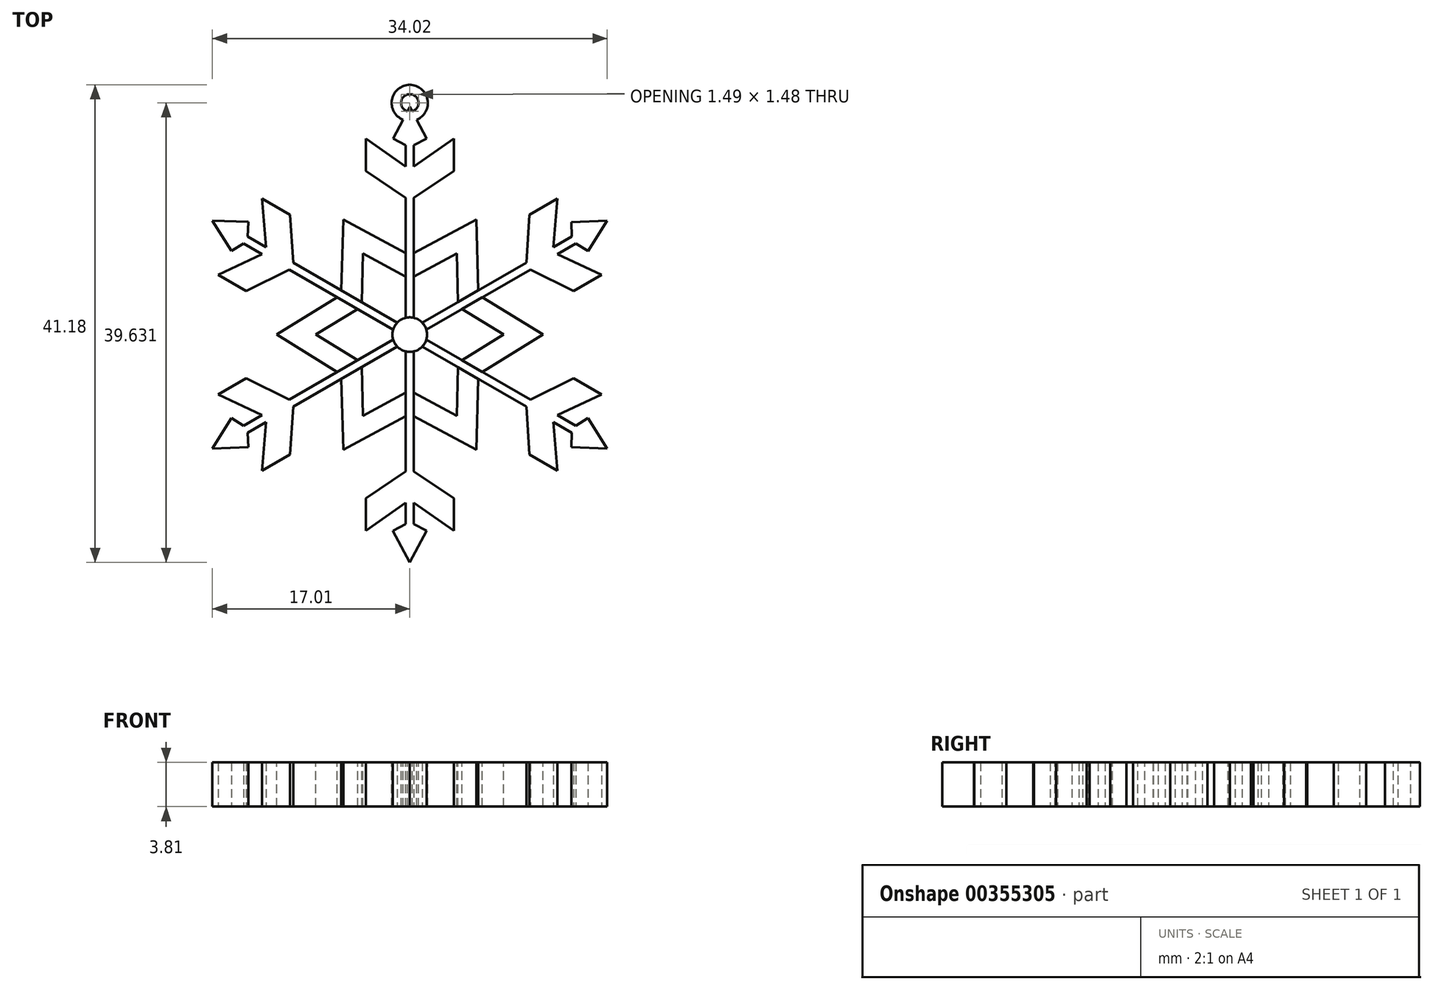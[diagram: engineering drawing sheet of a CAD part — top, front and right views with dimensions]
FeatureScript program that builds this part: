
annotation { "Feature Type Name" : "Feature", "Feature Type Description" : "" }
export const myFeature = defineFeature(function(context is Context, id is Id, definition is map)
    precondition{}
    {
        {
            var Q0;
            Q0=qCreatedBy(makeId("Top.planeOp"),FACE);
            var sketch = newSketch(context, id + "F0", { "sketchPlane" : qUnion([Q0])});
            skCircle(sketch, "E0", {"center": v(0, 0) * mm, "radius": 2.98 * mm});
            skLineSegment(sketch, "E1", {"start": v(0, -39.28) * mm, "end": v(2.88, -33.82) * mm});
            skLineSegment(sketch, "E2", {"start": v(2.88, -33.82) * mm, "end": v(-2.91, -33.82) * mm});
            skLineSegment(sketch, "E3", {"start": v(-2.91, -33.82) * mm, "end": v(0, -39.28) * mm});
            skLineSegment(sketch, "E4", {"start": v(0.7, -2.9) * mm, "end": v(0.7, -33.82) * mm});
            skLineSegment(sketch, "E5.MirrorCS", {"start": v(-0.7, -2.9) * mm, "end": v(-0.7, -33.82) * mm});
            skLineSegment(sketch, "E6", {"start": v(2.88, -33.82) * mm, "end": v(0.7, -32.67) * mm});
            skLineSegment(sketch, "E7", {"start": v(0.7, -29) * mm, "end": v(7.59, -33.78) * mm});
            skLineSegment(sketch, "E8", {"start": v(7.59, -33.78) * mm, "end": v(7.59, -28.23) * mm});
            skLineSegment(sketch, "E9", {"start": v(7.59, -28.23) * mm, "end": v(0.7, -23.6) * mm});
            skLineSegment(sketch, "E10.MirrorCS", {"start": v(-0.7, -29) * mm, "end": v(-7.59, -33.78) * mm});
            skLineSegment(sketch, "E11.MirrorCS", {"start": v(-7.59, -28.23) * mm, "end": v(-0.7, -23.6) * mm});
            skLineSegment(sketch, "E12.MirrorCS", {"start": v(-7.59, -33.78) * mm, "end": v(-7.59, -28.23) * mm});
            skLineSegment(sketch, "E13.MirrorCS", {"start": v(-2.88, -33.82) * mm, "end": v(-0.7, -32.67) * mm});
            skSolve(sketch);
        }
        {
            var Q0;
            Q0=qCreatedBy(makeId("Right.planeOp"),FACE);
            var sketch = newSketch(context, id + "F1", { "sketchPlane" : qUnion([Q0])});
            skLineSegment(sketch, "E14", {"start": v(0, 27.35) * mm, "end": v(0, -20.93) * mm});
            skSolve(sketch);
        }
        {
            var Q0;
            {var subQ0=sQuery(id+"F0.wireOp",EDGE,"E4");var subQ1=sQuery(id+"F0.wireOp",EDGE,"E0");var subQ2=makeQuery(id+"F0.imprint","INTERSECT",VERTEX,{"derivedFrom":[subQ1,subQ0]});Q0=makeQuery(id+"F0.imprint","IMPRINT",FACE,{"disambiguationData":[TD([[makeQuery(id+"F0.imprint","IMPRINT",EDGE,{"disambiguationData":[TD([[subQ2,1.0]])],"derivedFrom":subQ1}),-1.0]])]});}
            var Q1;
            {var subQ0=sQuery(id+"F0.wireOp",EDGE,"E10.MirrorCS");Q1=makeQuery(id+"F0.imprint","IMPRINT",FACE,{"disambiguationData":[TD([[makeQuery(id+"F0.imprint","IMPRINT",EDGE,{"derivedFrom":subQ0}),-1.0]])]});}
            var Q2;
            {var subQ0=sQuery(id+"F0.wireOp",EDGE,"E7");Q2=makeQuery(id+"F0.imprint","IMPRINT",FACE,{"disambiguationData":[TD([[makeQuery(id+"F0.imprint","IMPRINT",EDGE,{"derivedFrom":subQ0}),1.0]])]});}
            var Q3;
            {var subQ4=sQuery(id+"F0.wireOp",EDGE,"E1");Q3=makeQuery(id+"F0.imprint","IMPRINT",FACE,{"disambiguationData":[TD([[makeQuery(id+"F0.imprint","IMPRINT",EDGE,{"derivedFrom":subQ4}),1.0]])]});}
            var Q4;
            {var subQ0=sQuery(id+"F0.wireOp",EDGE,"E6");Q4=makeQuery(id+"F0.imprint","IMPRINT",FACE,{"disambiguationData":[TD([[makeQuery(id+"F0.imprint","IMPRINT",EDGE,{"derivedFrom":subQ0}),1.0]])]});}
            var Q5;
            {var subQ3=sQuery(id+"F0.wireOp",EDGE,"E13.MirrorCS");Q5=makeQuery(id+"F0.imprint","IMPRINT",FACE,{"disambiguationData":[TD([[makeQuery(id+"F0.imprint","IMPRINT",EDGE,{"derivedFrom":subQ3}),-1.0]])]});}
            extrude(context, id + "F2", {"entities" : qUnion([Q0, Q1, Q2, Q3, Q4, Q5]), "depth" : 7.62 * mm});
        }
        {
            var Q0;
            Q0=makeQuery(id+"F2.opExtrude","SWEPT_BODY",BODY,{"disambiguationData":[OSD([sQuery(id+"F0.wireOp",EDGE,"E0"),sQuery(id+"F0.wireOp",EDGE,"E1"),sQuery(id+"F0.wireOp",EDGE,"E2"),sQuery(id+"F0.wireOp",EDGE,"E3"),sQuery(id+"F0.wireOp",EDGE,"E4"),sQuery(id+"F0.wireOp",EDGE,"E5.MirrorCS"),sQuery(id+"F0.wireOp",EDGE,"E6"),sQuery(id+"F0.wireOp",EDGE,"E7"),sQuery(id+"F0.wireOp",EDGE,"E8"),sQuery(id+"F0.wireOp",EDGE,"E9"),sQuery(id+"F0.wireOp",EDGE,"E10.MirrorCS"),sQuery(id+"F0.wireOp",EDGE,"E11.MirrorCS"),sQuery(id+"F0.wireOp",EDGE,"E12.MirrorCS"),sQuery(id+"F0.wireOp",EDGE,"E13.MirrorCS")])]});
            var Q1;
            Q1=sQuery(id+"F1.wireOp",EDGE,"E14");
            circularPattern(context, id + "F3", {"entities" : qUnion([Q0]), "axis" : qUnion([Q1]), "angle" : 360 * degree, "instanceCount" : 6, "equalSpace" : true});
        }
        {
            var Q0;
            Q0=makeQuery(id+"F3.opPattern","COPY",FACE,{"derivedFrom":makeQuery(id+"F2.opExtrude","CAP_FACE",FACE,{"disambiguationData":[OSD([sQuery(id+"F0.wireOp",EDGE,"E0"),sQuery(id+"F0.wireOp",EDGE,"E1"),sQuery(id+"F0.wireOp",EDGE,"E2"),sQuery(id+"F0.wireOp",EDGE,"E3"),sQuery(id+"F0.wireOp",EDGE,"E4"),sQuery(id+"F0.wireOp",EDGE,"E5.MirrorCS"),sQuery(id+"F0.wireOp",EDGE,"E6"),sQuery(id+"F0.wireOp",EDGE,"E7"),sQuery(id+"F0.wireOp",EDGE,"E8"),sQuery(id+"F0.wireOp",EDGE,"E9"),sQuery(id+"F0.wireOp",EDGE,"E10.MirrorCS"),sQuery(id+"F0.wireOp",EDGE,"E11.MirrorCS"),sQuery(id+"F0.wireOp",EDGE,"E12.MirrorCS"),sQuery(id+"F0.wireOp",EDGE,"E13.MirrorCS")])],"isStart":false}),"instanceName":"1"});
            var sketch = newSketch(context, id + "F4", { "sketchPlane" : qUnion([Q0])});
            skLineSegment(sketch, "E15", {"start": v(-22.94, 0) * mm, "end": v(-12.52, -6.42) * mm});
            skLineSegment(sketch, "E16", {"start": v(-12.52, -6.42) * mm, "end": v(-8.99, -4.38) * mm});
            skLineSegment(sketch, "E17", {"start": v(-8.99, -4.38) * mm, "end": v(-16.2, 0) * mm});
            skLineSegment(sketch, "E18.MirrorCS", {"start": v(-22.94, 0) * mm, "end": v(-12.52, 6.42) * mm});
            skLineSegment(sketch, "E19.MirrorCS", {"start": v(-8.99, 4.38) * mm, "end": v(-16.2, 0) * mm});
            skLineSegment(sketch, "E20.MirrorCS", {"start": v(-12.52, 6.42) * mm, "end": v(-8.99, 4.38) * mm});
            skSolve(sketch);
        }
        {
            var Q0;
            Q0=makeQuery(id+"F4.imprint","IMPRINT",FACE,{"disambiguationData":[TD([[makeQuery(id+"F4.imprint","IMPRINT",EDGE,{"derivedFrom":sQuery(id+"F4.wireOp",EDGE,"E15")}),1.0]])]});
            extrude(context, id + "F5", {"entities" : qUnion([Q0]), "oppositeDirection" : true, "depth" : 7.62 * mm});
        }
        {
            var Q0;
            Q0=makeQuery(id+"F5.opExtrude","SWEPT_BODY",BODY,{"disambiguationData":[OSD([sQuery(id+"F4.wireOp",EDGE,"E15"),sQuery(id+"F4.wireOp",EDGE,"E16"),sQuery(id+"F4.wireOp",EDGE,"E17"),sQuery(id+"F4.wireOp",EDGE,"E18.MirrorCS"),sQuery(id+"F4.wireOp",EDGE,"E19.MirrorCS"),sQuery(id+"F4.wireOp",EDGE,"E20.MirrorCS")])]});
            var Q1;
            Q1=sQuery(id+"F1.wireOp",EDGE,"E14");
            circularPattern(context, id + "F6", {"entities" : qUnion([Q0]), "axis" : qUnion([Q1]), "angle" : 360 * degree, "instanceCount" : 6, "equalSpace" : true});
        }
        {
            var Q0;
            Q0=makeQuery(id+"F3.opPattern","COPY",FACE,{"derivedFrom":makeQuery(id+"F2.opExtrude","CAP_FACE",FACE,{"disambiguationData":[OSD([sQuery(id+"F0.wireOp",EDGE,"E0"),sQuery(id+"F0.wireOp",EDGE,"E1"),sQuery(id+"F0.wireOp",EDGE,"E2"),sQuery(id+"F0.wireOp",EDGE,"E3"),sQuery(id+"F0.wireOp",EDGE,"E4"),sQuery(id+"F0.wireOp",EDGE,"E5.MirrorCS"),sQuery(id+"F0.wireOp",EDGE,"E6"),sQuery(id+"F0.wireOp",EDGE,"E7"),sQuery(id+"F0.wireOp",EDGE,"E8"),sQuery(id+"F0.wireOp",EDGE,"E9"),sQuery(id+"F0.wireOp",EDGE,"E10.MirrorCS"),sQuery(id+"F0.wireOp",EDGE,"E11.MirrorCS"),sQuery(id+"F0.wireOp",EDGE,"E12.MirrorCS"),sQuery(id+"F0.wireOp",EDGE,"E13.MirrorCS")])],"isStart":false}),"instanceName":"3"});
            var sketch = newSketch(context, id + "F7", { "sketchPlane" : qUnion([Q0])});
            skCircle(sketch, "E21", {"center": v(0, 39.95) * mm, "radius": 1.5 * mm});
            skCircle(sketch, "E22", {"center": v(0, 39.95) * mm, "radius": 3.12 * mm});
            skSolve(sketch);
        }
        {
            var Q0;
            {var subQ0=sQuery(id+"F7.wireOp",EDGE,"E21");var subQ1=makeQuery(id+"F3.opPattern","COPY",EDGE,{"derivedFrom":makeQuery(id+"F2.opExtrude","CAP_EDGE",EDGE,{"disambiguationData":[OSD([sQuery(id+"F0.wireOp",EDGE,"E1")])],"isStart":false}),"instanceName":"3"});var subQ2=makeQuery(id+"F7.imprint","INTERSECT",VERTEX,{"derivedFrom":[subQ1,subQ0]});Q0=makeQuery(id+"F7.imprint","IMPRINT",FACE,{"disambiguationData":[TD([[makeQuery(id+"F7.imprint","IMPRINT",EDGE,{"disambiguationData":[TD([[subQ2,1.0]])],"derivedFrom":subQ0}),-1.0]])]});}
            extrude(context, id + "F8", {"entities" : qUnion([Q0]), "operationType" : NewBodyOperationType.ADD, "oppositeDirection" : true, "depth" : 7.62 * mm});
        }
        {
            var Q0;
            {var subQ0=sQuery(id+"F0.wireOp",EDGE,"E0");var subQ1=makeQuery(id+"F0.imprint","INTERSECT",VERTEX,{"derivedFrom":[subQ0,sQuery(id+"F0.wireOp",EDGE,"E4")]});Q0=makeQuery(id+"F0.imprint","IMPRINT",FACE,{"disambiguationData":[TD([[makeQuery(id+"F0.imprint","IMPRINT",EDGE,{"disambiguationData":[TD([[subQ1,1.0]])],"derivedFrom":subQ0}),1.0]])]});}
            extrude(context, id + "F9", {"entities" : qUnion([Q0]), "depth" : 7.62 * mm});
        }
        {
            var Q0;
            Q0=makeQuery(id+"F3.opPattern","COPY",BODY,{"derivedFrom":makeQuery(id+"F2.opExtrude","SWEPT_BODY",BODY,{"disambiguationData":[OSD([sQuery(id+"F0.wireOp",EDGE,"E0"),sQuery(id+"F0.wireOp",EDGE,"E1"),sQuery(id+"F0.wireOp",EDGE,"E2"),sQuery(id+"F0.wireOp",EDGE,"E3"),sQuery(id+"F0.wireOp",EDGE,"E4"),sQuery(id+"F0.wireOp",EDGE,"E5.MirrorCS"),sQuery(id+"F0.wireOp",EDGE,"E6"),sQuery(id+"F0.wireOp",EDGE,"E7"),sQuery(id+"F0.wireOp",EDGE,"E8"),sQuery(id+"F0.wireOp",EDGE,"E9"),sQuery(id+"F0.wireOp",EDGE,"E10.MirrorCS"),sQuery(id+"F0.wireOp",EDGE,"E11.MirrorCS"),sQuery(id+"F0.wireOp",EDGE,"E12.MirrorCS"),sQuery(id+"F0.wireOp",EDGE,"E13.MirrorCS")])]}),"instanceName":"3"});
            var Q1;
            Q1=makeQuery(id+"F6.opPattern","COPY",BODY,{"derivedFrom":makeQuery(id+"F5.opExtrude","SWEPT_BODY",BODY,{"disambiguationData":[OSD([sQuery(id+"F4.wireOp",EDGE,"E15"),sQuery(id+"F4.wireOp",EDGE,"E16"),sQuery(id+"F4.wireOp",EDGE,"E17"),sQuery(id+"F4.wireOp",EDGE,"E18.MirrorCS"),sQuery(id+"F4.wireOp",EDGE,"E19.MirrorCS"),sQuery(id+"F4.wireOp",EDGE,"E20.MirrorCS")])]}),"instanceName":"1"});
            var Q2;
            Q2=makeQuery(id+"F3.opPattern","COPY",BODY,{"derivedFrom":makeQuery(id+"F2.opExtrude","SWEPT_BODY",BODY,{"disambiguationData":[OSD([sQuery(id+"F0.wireOp",EDGE,"E0"),sQuery(id+"F0.wireOp",EDGE,"E1"),sQuery(id+"F0.wireOp",EDGE,"E2"),sQuery(id+"F0.wireOp",EDGE,"E3"),sQuery(id+"F0.wireOp",EDGE,"E4"),sQuery(id+"F0.wireOp",EDGE,"E5.MirrorCS"),sQuery(id+"F0.wireOp",EDGE,"E6"),sQuery(id+"F0.wireOp",EDGE,"E7"),sQuery(id+"F0.wireOp",EDGE,"E8"),sQuery(id+"F0.wireOp",EDGE,"E9"),sQuery(id+"F0.wireOp",EDGE,"E10.MirrorCS"),sQuery(id+"F0.wireOp",EDGE,"E11.MirrorCS"),sQuery(id+"F0.wireOp",EDGE,"E12.MirrorCS"),sQuery(id+"F0.wireOp",EDGE,"E13.MirrorCS")])]}),"instanceName":"2"});
            var Q3;
            Q3=makeQuery(id+"F5.opExtrude","SWEPT_BODY",BODY,{"disambiguationData":[OSD([sQuery(id+"F4.wireOp",EDGE,"E15"),sQuery(id+"F4.wireOp",EDGE,"E16"),sQuery(id+"F4.wireOp",EDGE,"E17"),sQuery(id+"F4.wireOp",EDGE,"E18.MirrorCS"),sQuery(id+"F4.wireOp",EDGE,"E19.MirrorCS"),sQuery(id+"F4.wireOp",EDGE,"E20.MirrorCS")])]});
            var Q4;
            Q4=makeQuery(id+"F3.opPattern","COPY",BODY,{"derivedFrom":makeQuery(id+"F2.opExtrude","SWEPT_BODY",BODY,{"disambiguationData":[OSD([sQuery(id+"F0.wireOp",EDGE,"E0"),sQuery(id+"F0.wireOp",EDGE,"E1"),sQuery(id+"F0.wireOp",EDGE,"E2"),sQuery(id+"F0.wireOp",EDGE,"E3"),sQuery(id+"F0.wireOp",EDGE,"E4"),sQuery(id+"F0.wireOp",EDGE,"E5.MirrorCS"),sQuery(id+"F0.wireOp",EDGE,"E6"),sQuery(id+"F0.wireOp",EDGE,"E7"),sQuery(id+"F0.wireOp",EDGE,"E8"),sQuery(id+"F0.wireOp",EDGE,"E9"),sQuery(id+"F0.wireOp",EDGE,"E10.MirrorCS"),sQuery(id+"F0.wireOp",EDGE,"E11.MirrorCS"),sQuery(id+"F0.wireOp",EDGE,"E12.MirrorCS"),sQuery(id+"F0.wireOp",EDGE,"E13.MirrorCS")])]}),"instanceName":"1"});
            var Q5;
            Q5=makeQuery(id+"F2.opExtrude","SWEPT_BODY",BODY,{"disambiguationData":[OSD([sQuery(id+"F0.wireOp",EDGE,"E0"),sQuery(id+"F0.wireOp",EDGE,"E1"),sQuery(id+"F0.wireOp",EDGE,"E2"),sQuery(id+"F0.wireOp",EDGE,"E3"),sQuery(id+"F0.wireOp",EDGE,"E4"),sQuery(id+"F0.wireOp",EDGE,"E5.MirrorCS"),sQuery(id+"F0.wireOp",EDGE,"E6"),sQuery(id+"F0.wireOp",EDGE,"E7"),sQuery(id+"F0.wireOp",EDGE,"E8"),sQuery(id+"F0.wireOp",EDGE,"E9"),sQuery(id+"F0.wireOp",EDGE,"E10.MirrorCS"),sQuery(id+"F0.wireOp",EDGE,"E11.MirrorCS"),sQuery(id+"F0.wireOp",EDGE,"E12.MirrorCS"),sQuery(id+"F0.wireOp",EDGE,"E13.MirrorCS")])]});
            var Q6;
            Q6=makeQuery(id+"F6.opPattern","COPY",BODY,{"derivedFrom":makeQuery(id+"F5.opExtrude","SWEPT_BODY",BODY,{"disambiguationData":[OSD([sQuery(id+"F4.wireOp",EDGE,"E15"),sQuery(id+"F4.wireOp",EDGE,"E16"),sQuery(id+"F4.wireOp",EDGE,"E17"),sQuery(id+"F4.wireOp",EDGE,"E18.MirrorCS"),sQuery(id+"F4.wireOp",EDGE,"E19.MirrorCS"),sQuery(id+"F4.wireOp",EDGE,"E20.MirrorCS")])]}),"instanceName":"4"});
            var Q7;
            Q7=makeQuery(id+"F6.opPattern","COPY",BODY,{"derivedFrom":makeQuery(id+"F5.opExtrude","SWEPT_BODY",BODY,{"disambiguationData":[OSD([sQuery(id+"F4.wireOp",EDGE,"E15"),sQuery(id+"F4.wireOp",EDGE,"E16"),sQuery(id+"F4.wireOp",EDGE,"E17"),sQuery(id+"F4.wireOp",EDGE,"E18.MirrorCS"),sQuery(id+"F4.wireOp",EDGE,"E19.MirrorCS"),sQuery(id+"F4.wireOp",EDGE,"E20.MirrorCS")])]}),"instanceName":"3"});
            var Q8;
            Q8=makeQuery(id+"F6.opPattern","COPY",BODY,{"derivedFrom":makeQuery(id+"F5.opExtrude","SWEPT_BODY",BODY,{"disambiguationData":[OSD([sQuery(id+"F4.wireOp",EDGE,"E15"),sQuery(id+"F4.wireOp",EDGE,"E16"),sQuery(id+"F4.wireOp",EDGE,"E17"),sQuery(id+"F4.wireOp",EDGE,"E18.MirrorCS"),sQuery(id+"F4.wireOp",EDGE,"E19.MirrorCS"),sQuery(id+"F4.wireOp",EDGE,"E20.MirrorCS")])]}),"instanceName":"2"});
            var Q9;
            Q9=makeQuery(id+"F3.opPattern","COPY",BODY,{"derivedFrom":makeQuery(id+"F2.opExtrude","SWEPT_BODY",BODY,{"disambiguationData":[OSD([sQuery(id+"F0.wireOp",EDGE,"E0"),sQuery(id+"F0.wireOp",EDGE,"E1"),sQuery(id+"F0.wireOp",EDGE,"E2"),sQuery(id+"F0.wireOp",EDGE,"E3"),sQuery(id+"F0.wireOp",EDGE,"E4"),sQuery(id+"F0.wireOp",EDGE,"E5.MirrorCS"),sQuery(id+"F0.wireOp",EDGE,"E6"),sQuery(id+"F0.wireOp",EDGE,"E7"),sQuery(id+"F0.wireOp",EDGE,"E8"),sQuery(id+"F0.wireOp",EDGE,"E9"),sQuery(id+"F0.wireOp",EDGE,"E10.MirrorCS"),sQuery(id+"F0.wireOp",EDGE,"E11.MirrorCS"),sQuery(id+"F0.wireOp",EDGE,"E12.MirrorCS"),sQuery(id+"F0.wireOp",EDGE,"E13.MirrorCS")])]}),"instanceName":"4"});
            var Q10;
            Q10=makeQuery(id+"F6.opPattern","COPY",BODY,{"derivedFrom":makeQuery(id+"F5.opExtrude","SWEPT_BODY",BODY,{"disambiguationData":[OSD([sQuery(id+"F4.wireOp",EDGE,"E15"),sQuery(id+"F4.wireOp",EDGE,"E16"),sQuery(id+"F4.wireOp",EDGE,"E17"),sQuery(id+"F4.wireOp",EDGE,"E18.MirrorCS"),sQuery(id+"F4.wireOp",EDGE,"E19.MirrorCS"),sQuery(id+"F4.wireOp",EDGE,"E20.MirrorCS")])]}),"instanceName":"5"});
            var Q11;
            Q11=makeQuery(id+"F3.opPattern","COPY",BODY,{"derivedFrom":makeQuery(id+"F2.opExtrude","SWEPT_BODY",BODY,{"disambiguationData":[OSD([sQuery(id+"F0.wireOp",EDGE,"E0"),sQuery(id+"F0.wireOp",EDGE,"E1"),sQuery(id+"F0.wireOp",EDGE,"E2"),sQuery(id+"F0.wireOp",EDGE,"E3"),sQuery(id+"F0.wireOp",EDGE,"E4"),sQuery(id+"F0.wireOp",EDGE,"E5.MirrorCS"),sQuery(id+"F0.wireOp",EDGE,"E6"),sQuery(id+"F0.wireOp",EDGE,"E7"),sQuery(id+"F0.wireOp",EDGE,"E8"),sQuery(id+"F0.wireOp",EDGE,"E9"),sQuery(id+"F0.wireOp",EDGE,"E10.MirrorCS"),sQuery(id+"F0.wireOp",EDGE,"E11.MirrorCS"),sQuery(id+"F0.wireOp",EDGE,"E12.MirrorCS"),sQuery(id+"F0.wireOp",EDGE,"E13.MirrorCS")])]}),"instanceName":"5"});
            var Q12;
            Q12=makeQuery(id+"F9.opExtrude","SWEPT_BODY",BODY,{"disambiguationData":[OSD([sQuery(id+"F0.wireOp",EDGE,"E0")])]});
            var Q13;
            Q13=sQuery(id+"F1.wireOp",VERTEX,"E14.end");
            transform(context, id + "F10", {"entities" : qUnion([Q0, Q1, Q2, Q3, Q4, Q5, Q6, Q7, Q8, Q9, Q10, Q11, Q12]), "transformType" : TransformType.SCALE_UNIFORMLY, "scale" : .5, "scalePoint" : qUnion([Q13]), "makeCopy" : false});
        }
    });
